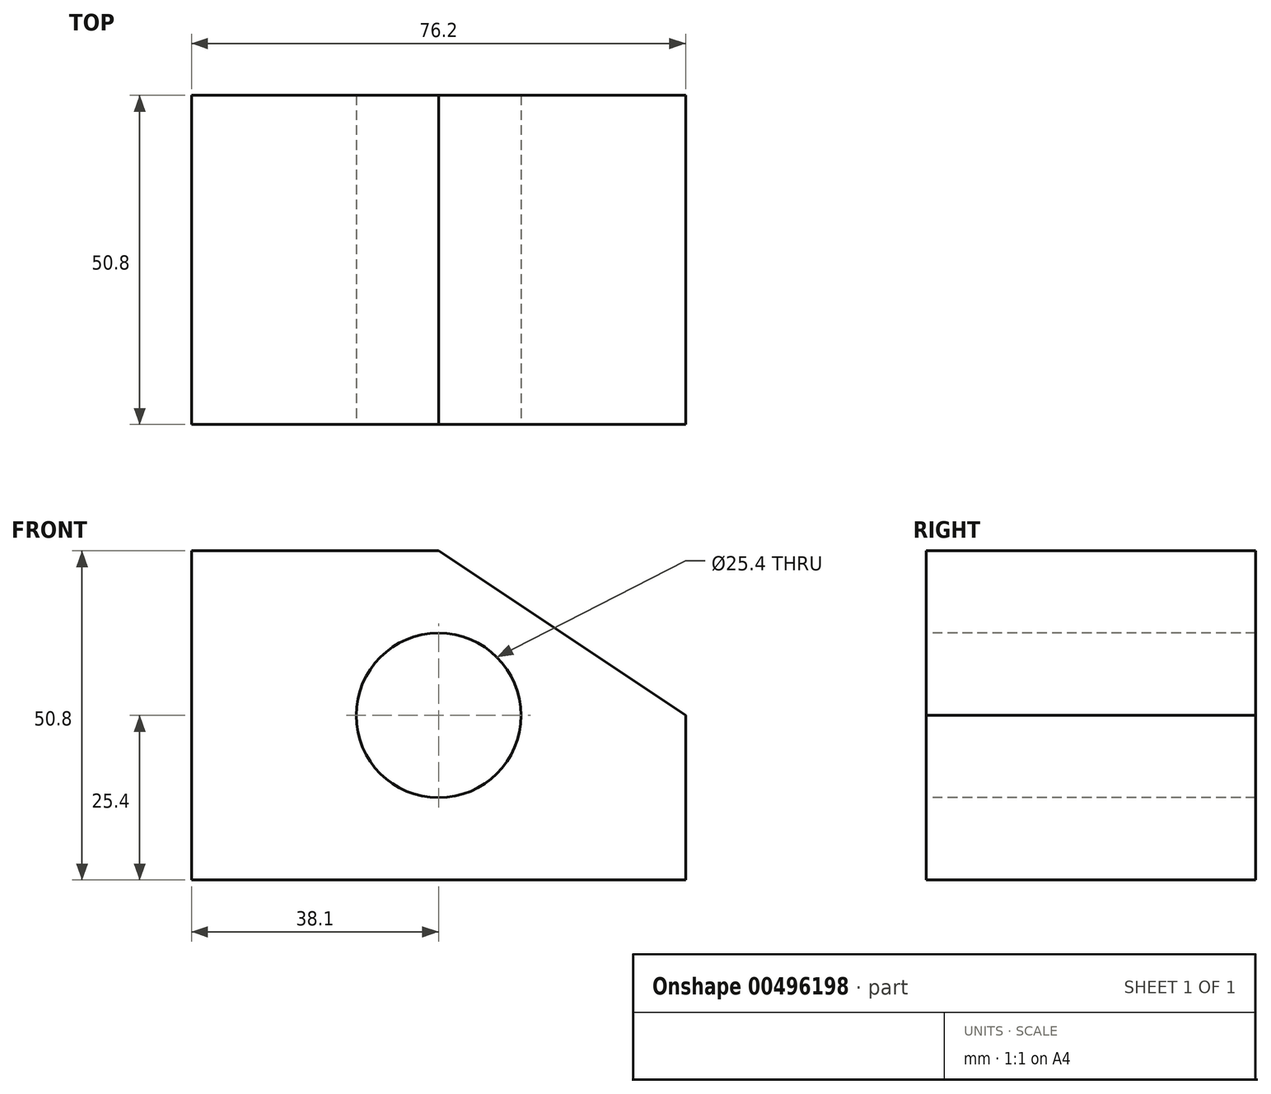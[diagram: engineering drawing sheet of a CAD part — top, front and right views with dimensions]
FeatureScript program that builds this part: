
annotation { "Feature Type Name" : "Feature", "Feature Type Description" : "" }
export const myFeature = defineFeature(function(context is Context, id is Id, definition is map)
    precondition{}
    {
        {
            var Q0;
            Q0=qCreatedBy(makeId("Top.planeOp"),FACE);
            var sketch = newSketch(context, id + "F0", { "sketchPlane" : qUnion([Q0])});
            skLineSegment(sketch, "E0.bottom", {"start": v(0, 0) * mm, "end": v(76.2, 0) * mm});
            skLineSegment(sketch, "E0.top", {"start": v(0, 50.8) * mm, "end": v(76.2, 50.8) * mm});
            skLineSegment(sketch, "E0.left", {"start": v(0, 0) * mm, "end": v(0, 50.8) * mm});
            skLineSegment(sketch, "E0.right", {"start": v(76.2, 0) * mm, "end": v(76.2, 50.8) * mm});
            skSolve(sketch);
        }
        {
            var Q0;
            Q0=makeQuery(id+"F0.imprint","IMPRINT",FACE,{"disambiguationData":[TD([[makeQuery(id+"F0.imprint","IMPRINT",EDGE,{"derivedFrom":sQuery(id+"F0.wireOp",EDGE,"E0.bottom")}),1.0]])]});
            extrude(context, id + "F1", {"entities" : qUnion([Q0]), "depth" : 50.8 * mm});
        }
        {
            var Q0;
            Q0=makeQuery(id+"F1.opExtrude","CAP_EDGE",EDGE,{"disambiguationData":[OSD([sQuery(id+"F0.wireOp",EDGE,"E0.right")])],"isStart":false});
            chamfer(context, id + "F2", {"entities" : qUnion([Q0]), "chamferType" : ChamferType.TWO_OFFSETS, "width1" : 38.1 * mm, "oppositeDirection" : false, "width2" : 25.4 * mm, "tangentPropagation" : true});
        }
        {
            var Q0;
            Q0=qCreatedBy(makeId("Front.planeOp"),FACE);
            var sketch = newSketch(context, id + "F3", { "sketchPlane" : qUnion([Q0])});
            skCircle(sketch, "E1", {"center": v(38.1, 25.4) * mm, "radius": 12.7 * mm});
            skSolve(sketch);
        }
        {
            var Q0;
            Q0 = qSketchRegion(id + "F3", true);
            extrude(context, id + "F4", {"entities" : qUnion([Q0]), "operationType" : NewBodyOperationType.REMOVE, "oppositeDirection" : true, "depth" : 50.8 * mm});
        }
    });
